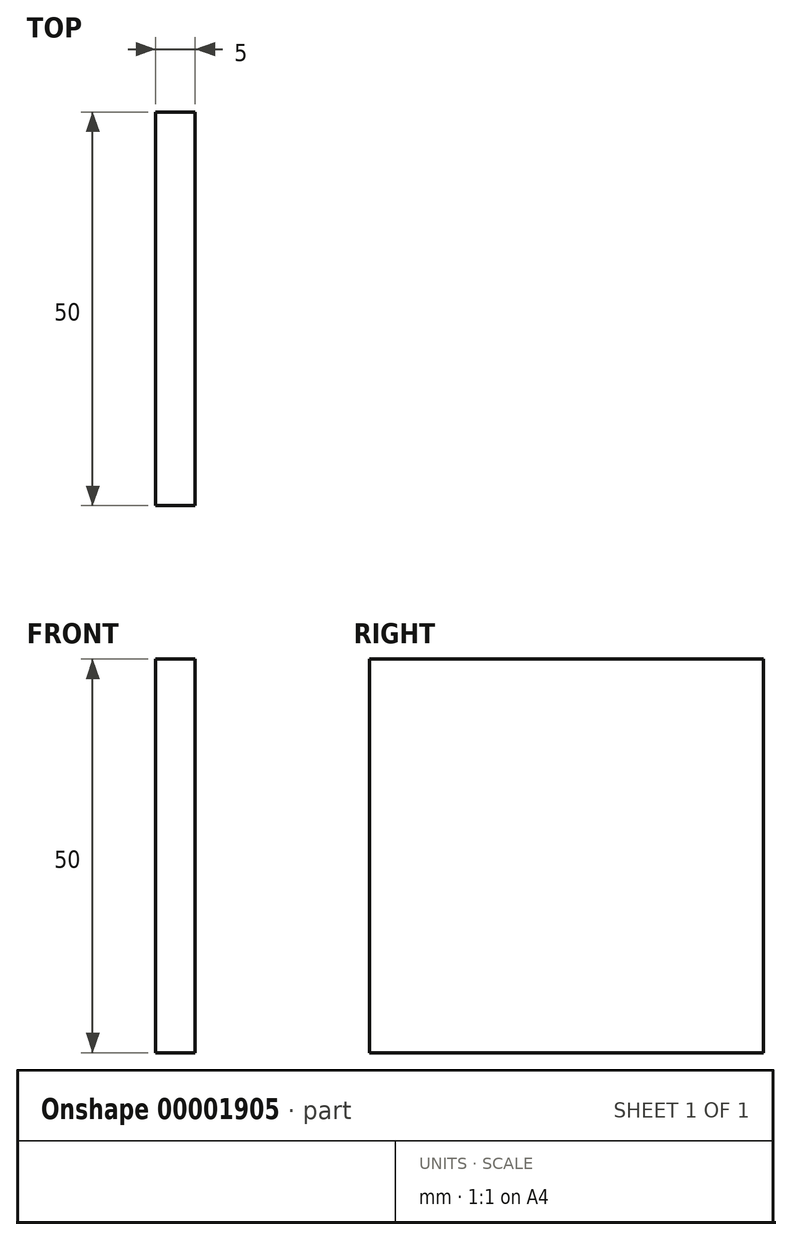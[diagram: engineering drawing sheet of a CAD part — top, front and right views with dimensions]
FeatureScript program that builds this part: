
annotation { "Feature Type Name" : "Feature", "Feature Type Description" : "" }
export const myFeature = defineFeature(function(context is Context, id is Id, definition is map)
    precondition{}
    {
        {
            var Q0;
            Q0=qCreatedBy(makeId("Right.planeOp"),FACE);
            var sketch = newSketch(context, id + "F0", { "sketchPlane" : qUnion([Q0])});
            skLineSegment(sketch, "E0.rect.bottom", {"start": v(25, -25) * mm, "end": v(-25, -25) * mm});
            skLineSegment(sketch, "E0.rect.top", {"start": v(25, 25) * mm, "end": v(-25, 25) * mm});
            skLineSegment(sketch, "E0.rect.left", {"start": v(25, -25) * mm, "end": v(25, 25) * mm});
            skLineSegment(sketch, "E0.rect.right", {"start": v(-25, -25) * mm, "end": v(-25, 25) * mm});
            skPoint(sketch, "E0.rect.middle", {"position": v(0, 0) * mm});
            skSolve(sketch);
        }
        {
            var Q0;
            Q0=makeQuery(id+"F0.imprint","IMPRINT",FACE,{"disambiguationData":[TD([[makeQuery(id+"F0.imprint","IMPRINT",EDGE,{"derivedFrom":sQuery(id+"F0.wireOp",EDGE,"E0.rect.bottom")}),-1.0]])]});
            extrude(context, id + "F1", {"entities" : qUnion([Q0]), "depth" : 5 * mm});
        }
    });
